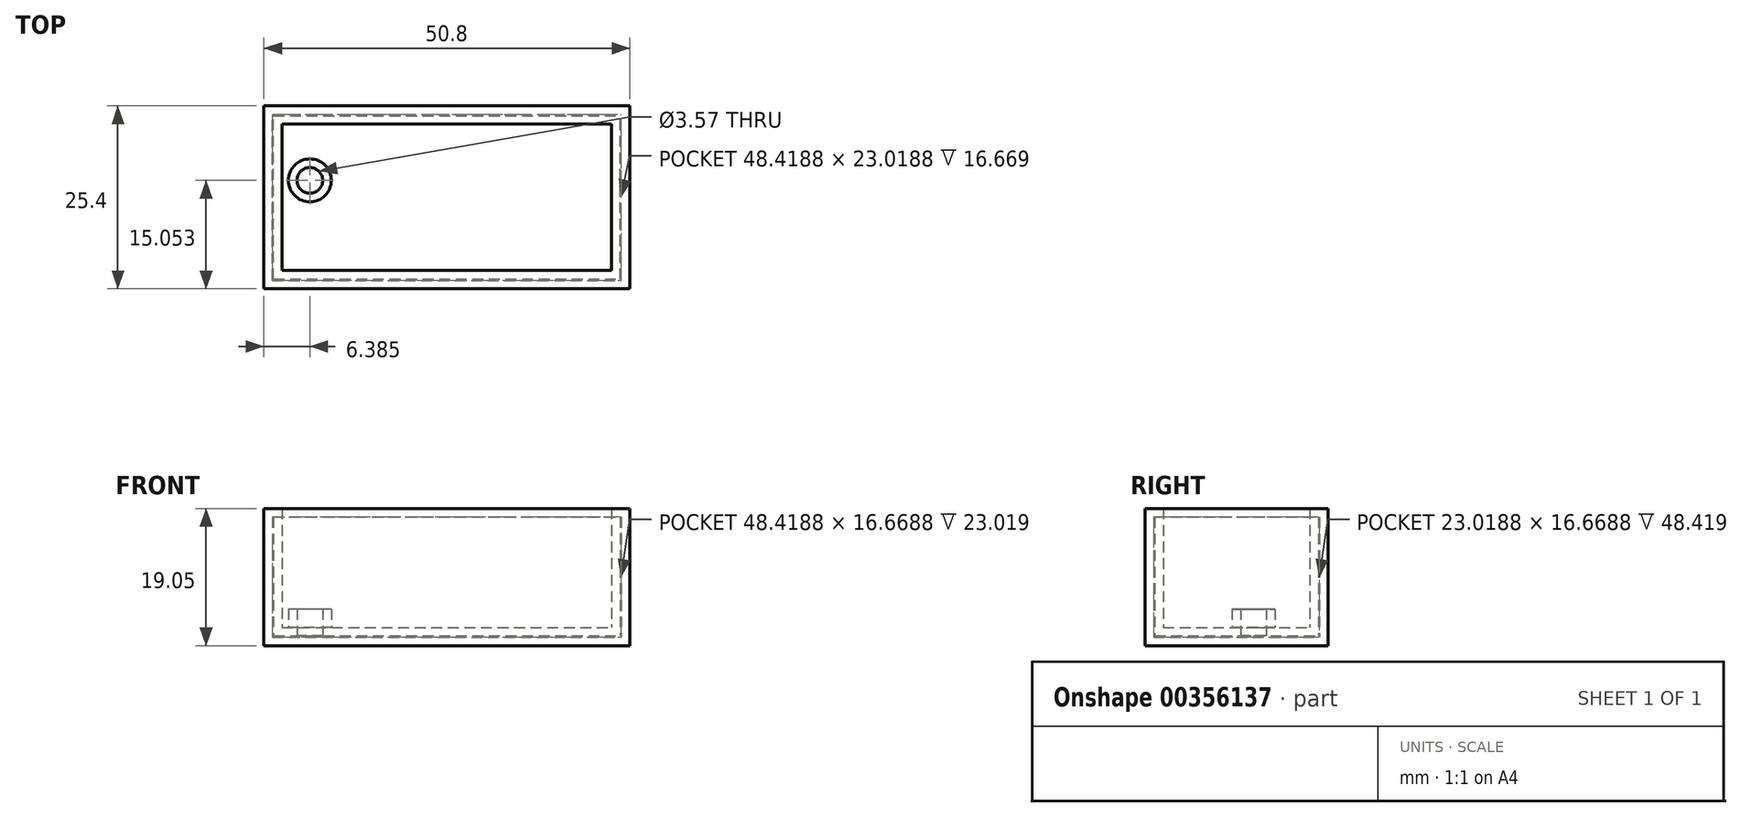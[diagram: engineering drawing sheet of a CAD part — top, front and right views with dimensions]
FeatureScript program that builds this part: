
annotation { "Feature Type Name" : "Feature", "Feature Type Description" : "" }
export const myFeature = defineFeature(function(context is Context, id is Id, definition is map)
    precondition{}
    {
        {
            var Q0;
            Q0=qCreatedBy(makeId("Top.planeOp"),FACE);
            var sketch = newSketch(context, id + "F0", { "sketchPlane" : qUnion([Q0])});
            skLineSegment(sketch, "E0.bottom", {"start": v(0, 0) * mm, "end": v(50.8, 0) * mm});
            skLineSegment(sketch, "E0.top", {"start": v(0, 25.4) * mm, "end": v(50.8, 25.4) * mm});
            skLineSegment(sketch, "E0.left", {"start": v(0, 0) * mm, "end": v(0, 25.4) * mm});
            skLineSegment(sketch, "E0.right", {"start": v(50.8, 0) * mm, "end": v(50.8, 25.4) * mm});
            skSolve(sketch);
        }
        {
            var Q0;
            Q0 = qSketchRegion(id + "F0", true);
            extrude(context, id + "F1", {"entities" : qUnion([Q0]), "depth" : 19.05 * mm});
        }
        {
            var Q0;
            Q0=makeQuery(id+"F1.opExtrude","CAP_FACE",FACE,{"disambiguationData":[OSD([sQuery(id+"F0.wireOp",EDGE,"E0.bottom"),sQuery(id+"F0.wireOp",EDGE,"E0.top"),sQuery(id+"F0.wireOp",EDGE,"E0.left"),sQuery(id+"F0.wireOp",EDGE,"E0.right")])],"isStart":false});
            shell(context, id + "F2", {"entities" : qUnion([Q0]), "thickness" : 2.54 * mm});
        }
        {
            var Q0;
            Q0=makeQuery(id+"F2.opShell","OFFSET_FACE",FACE,{"disambiguationData":[OSD([sQuery(id+"F0.wireOp",EDGE,"E0.bottom"),sQuery(id+"F0.wireOp",EDGE,"E0.top"),sQuery(id+"F0.wireOp",EDGE,"E0.left"),sQuery(id+"F0.wireOp",EDGE,"E0.right")])]});
            var sketch = newSketch(context, id + "F3", { "sketchPlane" : qUnion([Q0])});
            skCircle(sketch, "E1", {"center": v(6.39, 15.05) * mm, "radius": 2.98 * mm});
            skSolve(sketch);
        }
        {
            var Q0;
            Q0 = qSketchRegion(id + "F3", true);
            extrude(context, id + "F4", {"entities" : qUnion([Q0]), "operationType" : NewBodyOperationType.ADD, "depth" : 2.54 * mm});
        }
        {
            var Q0;
            Q0=makeQuery(id+"F4.opExtrude","CAP_FACE",FACE,{"disambiguationData":[OSD([sQuery(id+"F3.wireOp",EDGE,"E1")])],"isStart":false});
            shell(context, id + "F5", {"entities" : qUnion([Q0]), "thickness" : 1.2 * mm});
        }
    });
